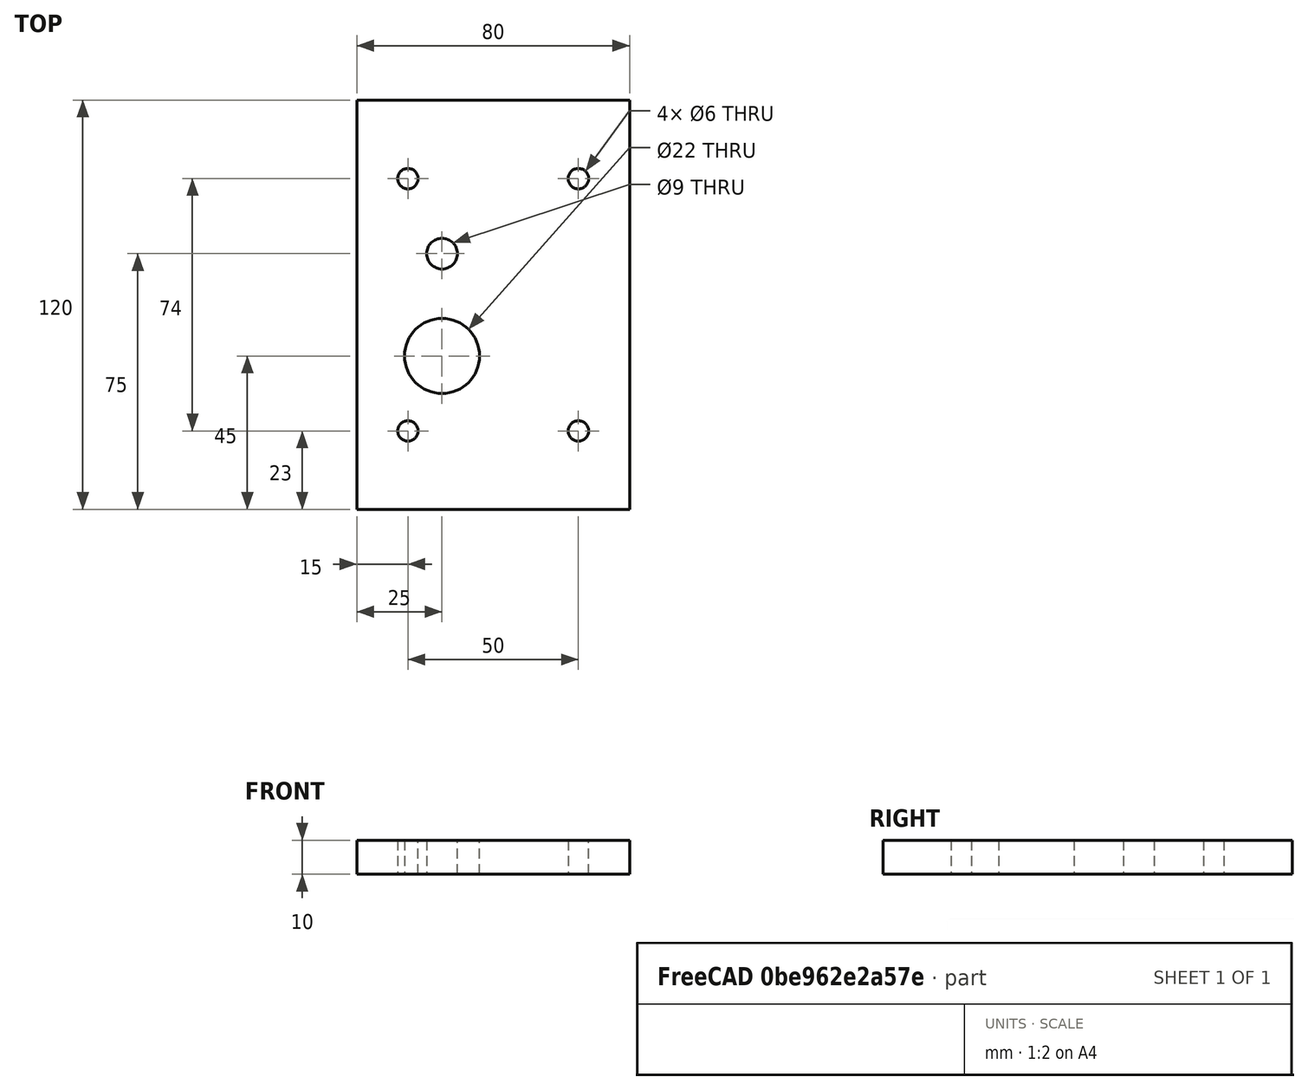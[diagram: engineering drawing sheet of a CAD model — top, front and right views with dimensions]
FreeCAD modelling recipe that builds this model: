
FCSTD DOCUMENT  (FreeCAD 0.19R24276 (Git))
Label: BLDC_holder_part3_middle_2
License: All rights reserved
LicenseURL: http://en.wikipedia.org/wiki/All_rights_reserved
objects: Sketcher::SketchObject×1, PartDesign::Pad×1, PartDesign::Body×1
note: 4 computed .brp shape members not serialized (recipe doc carries the construction recipe); baked Part::Feature solids carry a one-line shape summary decoded from their .brp

FEATURE [Sketcher::SketchObject] Sketch  label="Sketch_L80x120"
  FullyConstrained = false
  MapMode = 5
  Support = -> [XY_Plane]
  sketch-geometry (26):
    g0: Circle CenterX=0 CenterY=0 CenterZ=0 NormalX=0 NormalY=0 NormalZ=1 AngleXU=0 Radius=4.5
    g1: Circle CenterX=0 CenterY=-30 CenterZ=0 NormalX=0 NormalY=0 NormalZ=1 AngleXU=0 Radius=11
    g2: LineSegment StartX=-25 StartY=45 StartZ=0 EndX=55 EndY=45 EndZ=0
    g3: LineSegment StartX=55 StartY=45 StartZ=0 EndX=55 EndY=-75 EndZ=0
    g4: LineSegment StartX=55 StartY=-75 StartZ=0 EndX=-25 EndY=-75 EndZ=0
    g5: LineSegment StartX=-25 StartY=-75 StartZ=0 EndX=-25 EndY=45 EndZ=0
    g6: Circle CenterX=-10 CenterY=-52 CenterZ=0 NormalX=0 NormalY=0 NormalZ=1 AngleXU=0 Radius=3
    g7: Circle CenterX=40 CenterY=-52 CenterZ=0 NormalX=0 NormalY=0 NormalZ=1 AngleXU=0 Radius=3
    g8: Circle CenterX=40 CenterY=22 CenterZ=0 NormalX=0 NormalY=0 NormalZ=1 AngleXU=0 Radius=3
    g9: Circle CenterX=-10 CenterY=22 CenterZ=0 NormalX=0 NormalY=0 NormalZ=1 AngleXU=0 Radius=3
    g10: Circle CenterX=0 CenterY=0 CenterZ=0 NormalX=0 NormalY=0 NormalZ=1 AngleXU=0 Radius=11
    g11: LineSegment StartX=14.5 StartY=-15.5 StartZ=0 EndX=-14.5 EndY=-15.5 EndZ=0
    g12: LineSegment StartX=-14.5 StartY=-15.5 StartZ=0 EndX=-14.5 EndY=-44.5 EndZ=0
    g13: LineSegment StartX=-14.5 StartY=-44.5 StartZ=0 EndX=14.5 EndY=-44.5 EndZ=0
    g14: LineSegment StartX=14.5 StartY=-44.5 StartZ=0 EndX=14.5 EndY=-15.5 EndZ=0
    g15: Circle CenterX=0 CenterY=-30 CenterZ=0 NormalX=0 NormalY=0 NormalZ=1 AngleXU=0 Radius=20.5061
    g16: LineSegment StartX=-44.3555 StartY=-59 StartZ=0 EndX=66.9363 EndY=-59 EndZ=0
    g17: LineSegment StartX=66.9363 StartY=-59 StartZ=0 EndX=66.9363 EndY=-67 EndZ=0
    g18: LineSegment StartX=66.9363 StartY=-67 StartZ=0 EndX=-44.3555 EndY=-67 EndZ=0
    g19: LineSegment StartX=-44.3555 StartY=-67 StartZ=0 EndX=-44.3555 EndY=-59 EndZ=0
    g20: LineSegment StartX=-44.3555 StartY=-63 StartZ=0 EndX=70.3737 EndY=-63 EndZ=0
    g21: LineSegment StartX=-44.3555 StartY=29 StartZ=0 EndX=66.9363 EndY=29 EndZ=0
    g22: LineSegment StartX=66.9363 StartY=29 StartZ=0 EndX=66.9363 EndY=37 EndZ=0
    g23: LineSegment StartX=66.9363 StartY=37 StartZ=0 EndX=-44.3555 EndY=37 EndZ=0
    g24: LineSegment StartX=-44.3555 StartY=37 StartZ=0 EndX=-44.3555 EndY=29 EndZ=0
    g25: LineSegment StartX=-44.3555 StartY=33 StartZ=0 EndX=70.3737 EndY=33 EndZ=0
  constraints (67):
    c: Coincident(g0,g-1)
    c: Diameter(g0) = 9
    c: PointOnObject(g1,g-2)
    c: Diameter(g1) = 22
    c: DistanceY(g1,g0) = 30
    c: Coincident(g2,g3)
    c: Coincident(g3,g4)
    c: Coincident(g4,g5)
    c: Coincident(g5,g2)
    c: Horizontal(g2)
    c: Horizontal(g4)
    c: Vertical(g3)
    c: Vertical(g5)
    c: DistanceY(g4,g1) = 45
    c: DistanceY(g3,g2) = 120
    c: Horizontal(g9,g8)
    c: Horizontal(g6,g7)
    c: Vertical(g9,g6)
    c: Vertical(g8,g7)
    c: Diameter(g6) = 6
    c: Equal(g6,g8)
    c: Equal(g6,g9)
    c: Equal(g6,g7)
    c: DistanceY(g6,g1) = 22
    c: DistanceY(g0,g9) = 22
    c: Coincident(g10,g0)
    c: Diameter(g10) = 22
    c: DistanceX(g7,g3) = 15
    c: DistanceX(g4,g6) = 15
    c: DistanceX(g2,g2) = 80
    c: Coincident(g11,g12)
    c: Coincident(g12,g13)
    c: Coincident(g13,g14)
    c: Coincident(g14,g11)
    c: Equal(g11,g12)
    c: Equal(g11,g13)
    c: Equal(g11,g14)
    c: PointOnObject(g11,g15)
    c: PointOnObject(g12,g15)
    c: PointOnObject(g13,g15)
    c: PointOnObject(g14,g15)
    c: Coincident(g15,g1)
    c: DistanceY(g14,g14) = 29
    c: Vertical(g14)
    c: DistanceX(g2,g0) = 25
    c: Coincident(g16,g17)
    c: Coincident(g17,g18)
    c: Coincident(g18,g19)
    c: Coincident(g19,g16)
    c: Horizontal(g16)
    c: Horizontal(g18)
    c: Vertical(g17)
    c: Vertical(g19)
    c: Horizontal(g20)
    c: Symmetric(g16,g18,g20)
    c: DistanceY(g4,g20) = 12
    c: DistanceY(g19,g19) = 8
    c: Coincident(g21,g22)
    c: Coincident(g22,g23)
    c: Coincident(g23,g24)
    c: Coincident(g24,g21)
    c: Symmetric(g21,g23,g25)
    c: DistanceY(g25,g2) = 12
    c: Horizontal(g23)
    c: Horizontal(g21)
    c: Horizontal(g25)
    c: DistanceY(g24,g24) = 8
FEATURE [PartDesign::Pad] Pad  label="Pad_h10"
  Direction = (1,1,1)
  Length = 10
  Length2 = 100
  Profile = -> Sketch
  Type = 0
FEATURE [PartDesign::Body] Body
  Group = -> [Sketch,Pad]
  Origin = -> Origin
  Tip = -> Pad
